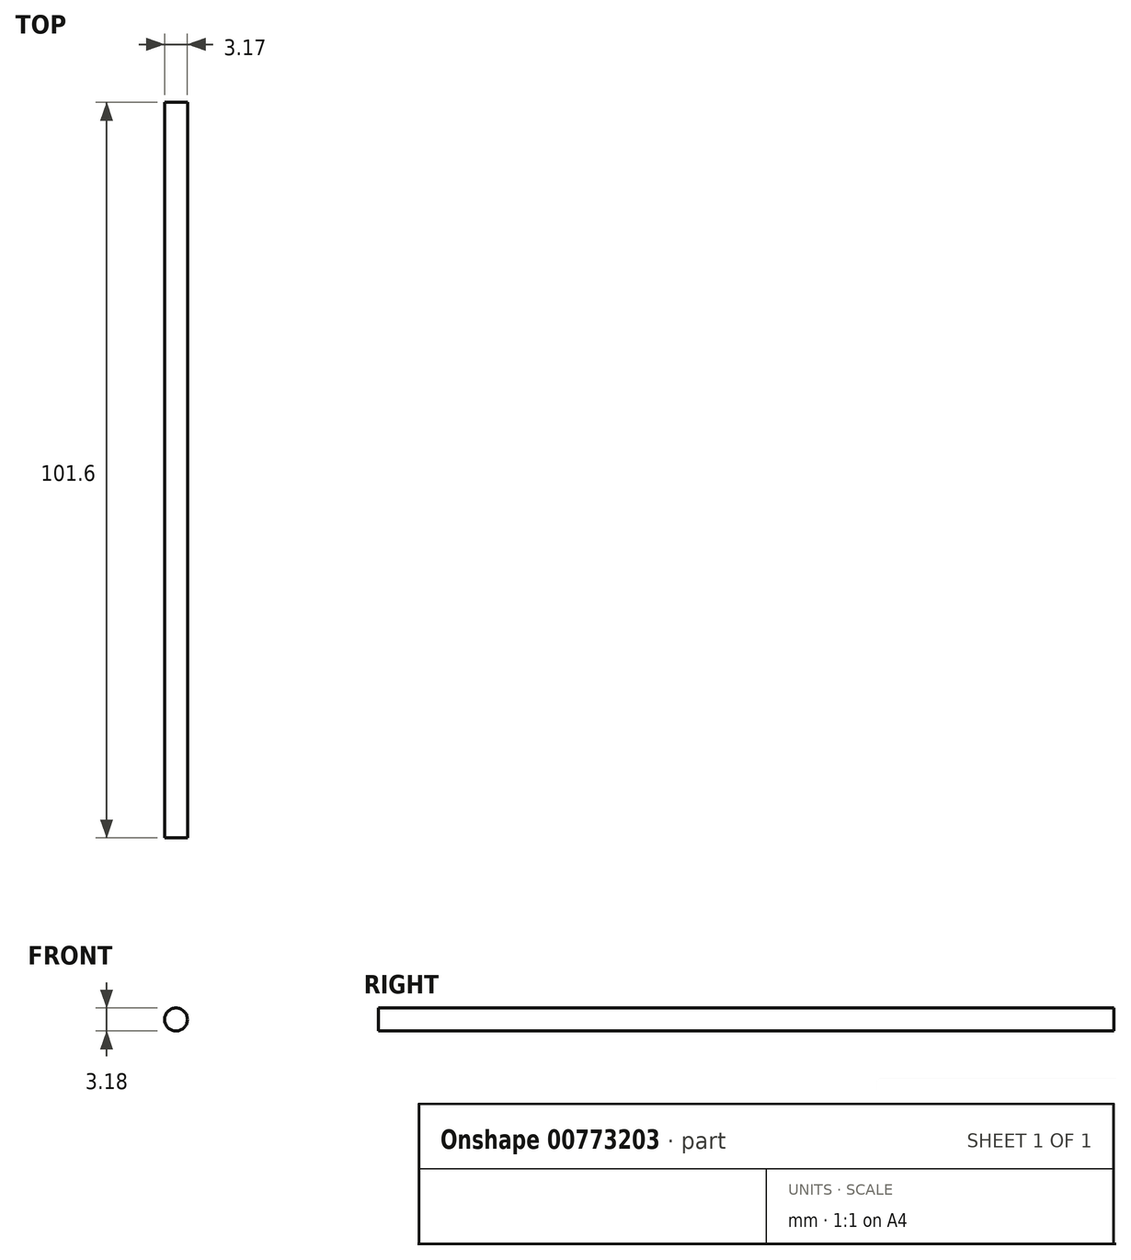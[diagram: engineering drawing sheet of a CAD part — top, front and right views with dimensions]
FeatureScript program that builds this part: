
annotation { "Feature Type Name" : "Feature", "Feature Type Description" : "" }
export const myFeature = defineFeature(function(context is Context, id is Id, definition is map)
    precondition{}
    {
        {
            var Q0;
            Q0=qCreatedBy(makeId("Front.planeOp"),FACE);
            var sketch = newSketch(context, id + "F0", { "sketchPlane" : qUnion([Q0])});
            skCircle(sketch, "E0", {"center": v(-6.26, 0) * mm, "radius": 1.59 * mm});
            skSolve(sketch);
        }
        {
            var Q0;
            Q0 = qSketchRegion(id + "F0", true);
            extrude(context, id + "F1", {"entities" : qUnion([Q0]), "depth" : 101.6 * mm, "offsetDistance" : 25.4 * mm});
        }
    });
